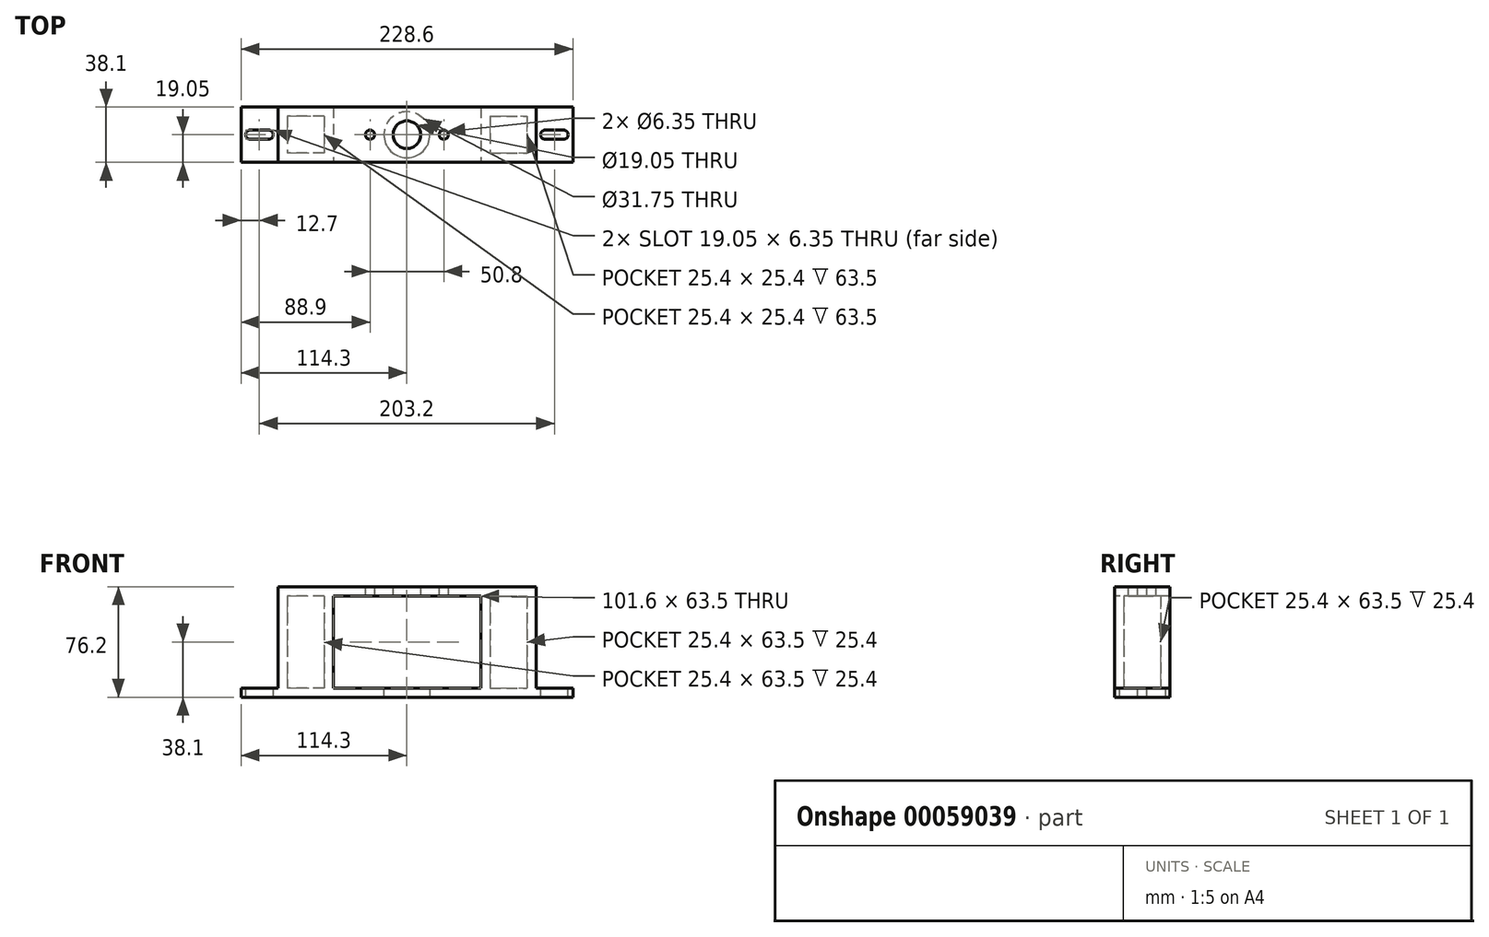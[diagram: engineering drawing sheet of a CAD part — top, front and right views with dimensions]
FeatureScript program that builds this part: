
annotation { "Feature Type Name" : "Feature", "Feature Type Description" : "" }
export const myFeature = defineFeature(function(context is Context, id is Id, definition is map)
    precondition{}
    {
        {
            var Q0;
            Q0=qCreatedBy(makeId("Top.planeOp"),FACE);
            var sketch = newSketch(context, id + "F0", { "sketchPlane" : qUnion([Q0])});
            skLineSegment(sketch, "E0.rect.bottom", {"start": v(114.3, 19.05) * mm, "end": v(-114.3, 19.05) * mm});
            skLineSegment(sketch, "E0.rect.top", {"start": v(114.3, -19.05) * mm, "end": v(-114.3, -19.05) * mm});
            skLineSegment(sketch, "E0.rect.left", {"start": v(114.3, 19.05) * mm, "end": v(114.3, -19.05) * mm});
            skLineSegment(sketch, "E0.rect.right", {"start": v(-114.3, 19.05) * mm, "end": v(-114.3, -19.05) * mm});
            skPoint(sketch, "E0.rect.middle", {"position": v(0, 0) * mm});
            skSolve(sketch);
        }
        {
            var Q0;
            Q0=qSketchRegion(id+"F0",true);
            extrude(context, id + "F9", {"entities" : qUnion([Q0]), "depth" : 6.35 * mm});
        }
        {
            var Q0;
            Q0=makeQuery(id+"F9.opExtrude","CAP_FACE",FACE,{"disambiguationData":[OSD([sQuery(id+"F0.wireOp",EDGE,"E0.rect.bottom"),sQuery(id+"F0.wireOp",EDGE,"E0.rect.top"),sQuery(id+"F0.wireOp",EDGE,"E0.rect.left"),sQuery(id+"F0.wireOp",EDGE,"E0.rect.right")])],"isStart":false});
            var sketch = newSketch(context, id + "F1", { "sketchPlane" : qUnion([Q0])});
            skLineSegment(sketch, "E1.bottom", {"start": v(88.9, 19.05) * mm, "end": v(50.8, 19.05) * mm});
            skLineSegment(sketch, "E1.top", {"start": v(88.9, -19.05) * mm, "end": v(50.8, -19.05) * mm});
            skLineSegment(sketch, "E1.left", {"start": v(88.9, 19.05) * mm, "end": v(88.9, -19.05) * mm});
            skLineSegment(sketch, "E1.right", {"start": v(50.8, 19.05) * mm, "end": v(50.8, -19.05) * mm});
            skLineSegment(sketch, "E2.bottom", {"start": v(57.15, 12.7) * mm, "end": v(82.55, 12.7) * mm});
            skLineSegment(sketch, "E2.top", {"start": v(57.15, -12.7) * mm, "end": v(82.55, -12.7) * mm});
            skLineSegment(sketch, "E2.left", {"start": v(57.15, 12.7) * mm, "end": v(57.15, -12.7) * mm});
            skLineSegment(sketch, "E2.right", {"start": v(82.55, 12.7) * mm, "end": v(82.55, -12.7) * mm});
            skLineSegment(sketch, "E3.MirrorCS", {"start": v(-50.8, 19.05) * mm, "end": v(-50.8, -19.05) * mm});
            skLineSegment(sketch, "E4.MirrorCS", {"start": v(-57.15, 12.7) * mm, "end": v(-57.15, -12.7) * mm});
            skLineSegment(sketch, "E5.MirrorCS", {"start": v(-88.9, -19.05) * mm, "end": v(-50.8, -19.05) * mm});
            skLineSegment(sketch, "E6.MirrorCS", {"start": v(-57.15, -12.7) * mm, "end": v(-82.55, -12.7) * mm});
            skLineSegment(sketch, "E7.MirrorCS", {"start": v(-57.15, 12.7) * mm, "end": v(-82.55, 12.7) * mm});
            skLineSegment(sketch, "E8.MirrorCS", {"start": v(-88.9, 19.05) * mm, "end": v(-50.8, 19.05) * mm});
            skLineSegment(sketch, "E9.MirrorCS", {"start": v(-82.55, 12.7) * mm, "end": v(-82.55, -12.7) * mm});
            skLineSegment(sketch, "E10.MirrorCS", {"start": v(-88.9, 19.05) * mm, "end": v(-88.9, -19.05) * mm});
            skPoint(sketch, "E11.end.orphan", {"position": v(0, 19.05) * mm});
            skSolve(sketch);
        }
        {
            var Q0;
            Q0=qSketchRegion(id+"F1",true);
            extrude(context, id + "F10", {"entities" : qUnion([Q0]), "operationType" : NewBodyOperationType.ADD, "depth" : 63.5 * mm});
        }
        {
            var Q0;
            Q0=makeQuery(id+"F10.opExtrude","CAP_FACE",FACE,{"disambiguationData":[OSD([sQuery(id+"F1.wireOp",EDGE,"E1.bottom"),sQuery(id+"F1.wireOp",EDGE,"E1.top"),sQuery(id+"F1.wireOp",EDGE,"E1.left"),sQuery(id+"F1.wireOp",EDGE,"E1.right"),sQuery(id+"F1.wireOp",EDGE,"E2.bottom"),sQuery(id+"F1.wireOp",EDGE,"E2.top"),sQuery(id+"F1.wireOp",EDGE,"E2.right"),sQuery(id+"F1.wireOp",EDGE,"E2.left")])],"isStart":false});
            var sketch = newSketch(context, id + "F11", { "sketchPlane" : qUnion([Q0])});
            skLineSegment(sketch, "E12.bottom", {"start": v(88.9, 19.05) * mm, "end": v(-88.9, 19.05) * mm});
            skLineSegment(sketch, "E12.top", {"start": v(88.9, -19.05) * mm, "end": v(-88.9, -19.05) * mm});
            skLineSegment(sketch, "E12.left", {"start": v(88.9, 19.05) * mm, "end": v(88.9, -19.05) * mm});
            skLineSegment(sketch, "E12.right", {"start": v(-88.9, 19.05) * mm, "end": v(-88.9, -19.05) * mm});
            skSolve(sketch);
        }
        {
            var Q0;
            Q0=qSketchRegion(id+"F11",true);
            extrude(context, id + "F2", {"entities" : qUnion([Q0]), "operationType" : NewBodyOperationType.ADD, "depth" : 6.35 * mm});
        }
        {
            var Q0;
            Q0=makeQuery(id+"F2.opExtrude","CAP_FACE",FACE,{"disambiguationData":[OSD([sQuery(id+"F11.wireOp",EDGE,"E12.bottom"),sQuery(id+"F11.wireOp",EDGE,"E12.top"),sQuery(id+"F11.wireOp",EDGE,"E12.left"),sQuery(id+"F11.wireOp",EDGE,"E12.right")])],"isStart":false});
            var sketch = newSketch(context, id + "F3", { "sketchPlane" : qUnion([Q0])});
            skCircle(sketch, "E13", {"center": v(0, 0) * mm, "radius": 9.53 * mm});
            skCircle(sketch, "E14", {"center": v(25.4, 0) * mm, "radius": 3.18 * mm});
            skCircle(sketch, "E15", {"center": v(-25.4, 0) * mm, "radius": 3.18 * mm});
            skSolve(sketch);
        }
        {
            var Q0;
            Q0=qSketchRegion(id+"F3",true);
            extrude(context, id + "F4", {"entities" : qUnion([Q0]), "operationType" : NewBodyOperationType.REMOVE, "oppositeDirection" : true, "depth" : 25.4 * mm});
        }
        {
            var Q0;
            {var subQ0=sQuery(id+"F0.wireOp",EDGE,"E0.rect.right");var subQ1=sQuery(id+"F0.wireOp",EDGE,"E0.rect.top");var subQ2=sQuery(id+"F0.wireOp",EDGE,"E0.rect.bottom");Q0=makeQuery(id+"F10.boolean.opBoolean","SPLIT",FACE,{"disambiguationData":[TD([makeQuery(id+"F9.opExtrude","SWEPT_FACE",FACE,{"disambiguationData":[OSD([subQ0])]})])],"derivedFrom":makeQuery(id+"F9.opExtrude","CAP_FACE",FACE,{"disambiguationData":[OSD([subQ2,subQ1,sQuery(id+"F0.wireOp",EDGE,"E0.rect.left"),subQ0])],"isStart":false})});}
            var sketch = newSketch(context, id + "F5", { "sketchPlane" : qUnion([Q0])});
            skLineSegment(sketch, "E16", {"start": v(-107.95, 3.18) * mm, "end": v(-95.25, 3.18) * mm});
            skLineSegment(sketch, "E17", {"start": v(-107.95, -3.17) * mm, "end": v(-95.25, -3.17) * mm});
            skArc(sketch, "E18", {"start": v(-95.25, 3.18) * mm, "mid": v(-92.08, 0) * mm, "end": v(-95.25, -3.17) * mm});
            skArc(sketch, "E19", {"start": v(-107.95, 3.18) * mm, "mid": v(-111.13, 0) * mm, "end": v(-107.95, -3.17) * mm});
            skLineSegment(sketch, "E20", {"start": v(0, 0) * mm, "end": v(0, -15.88) * mm});
            skLineSegment(sketch, "E21.MirrorCS", {"start": v(107.95, -3.17) * mm, "end": v(95.25, -3.17) * mm});
            skLineSegment(sketch, "E22.MirrorCS", {"start": v(107.95, 3.18) * mm, "end": v(95.25, 3.18) * mm});
            skArc(sketch, "E23.MirrorCS", {"start": v(95.25, 3.18) * mm, "mid": v(92.08, 0) * mm, "end": v(95.25, -3.17) * mm});
            skArc(sketch, "E24.MirrorCS", {"start": v(107.95, 3.18) * mm, "mid": v(111.13, 0) * mm, "end": v(107.95, -3.17) * mm});
            skSolve(sketch);
        }
        {
            var Q0;
            Q0=qSketchRegion(id+"F5",true);
            extrude(context, id + "F6", {"entities" : qUnion([Q0]), "operationType" : NewBodyOperationType.REMOVE, "endBound" : BoundingType.THROUGH_ALL, "oppositeDirection" : true, "depth" : 25.4 * mm});
        }
        {
            var Q0;
            Q0=makeQuery(id+"F9.opExtrude","CAP_FACE",FACE,{"disambiguationData":[OSD([sQuery(id+"F0.wireOp",EDGE,"E0.rect.bottom"),sQuery(id+"F0.wireOp",EDGE,"E0.rect.top"),sQuery(id+"F0.wireOp",EDGE,"E0.rect.left"),sQuery(id+"F0.wireOp",EDGE,"E0.rect.right")])],"isStart":true});
            var sketch = newSketch(context, id + "F7", { "sketchPlane" : qUnion([Q0])});
            skCircle(sketch, "E25", {"center": v(0, 0) * mm, "radius": 15.88 * mm});
            skSolve(sketch);
        }
        {
            var Q0;
            Q0=makeQuery(id+"F7.imprint","IMPRINT",FACE,{"disambiguationData":[TD([[makeQuery(id+"F7.imprint","IMPRINT",EDGE,{"derivedFrom":sQuery(id+"F7.wireOp",EDGE,"E25")}),1.0]])]});
            extrude(context, id + "F8", {"entities" : qUnion([Q0]), "operationType" : NewBodyOperationType.REMOVE, "oppositeDirection" : true, "depth" : 25.4 * mm});
        }
    });
